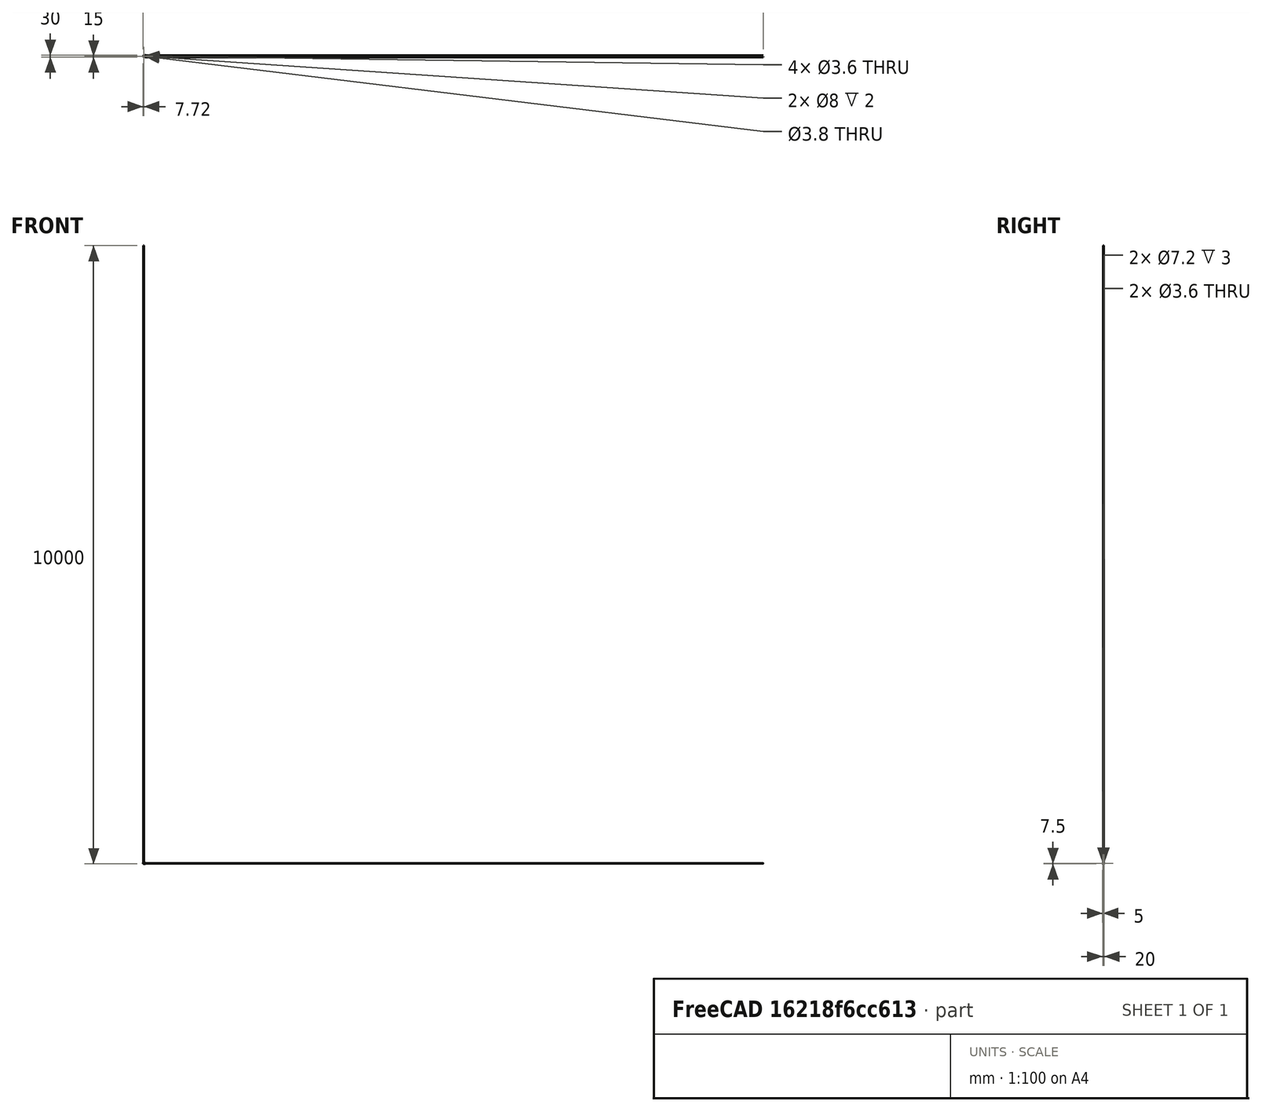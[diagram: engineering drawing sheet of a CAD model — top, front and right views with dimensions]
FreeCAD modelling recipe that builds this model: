
FCSTD DOCUMENT  (FreeCAD 0.15R4671 (Git))
Label: BedLevelingBracket
License: All rights reserved
LicenseURL: http://en.wikipedia.org/wiki/All_rights_reserved
objects: Sketcher::SketchObject×7, PartDesign::Pocket×5, Mesh::Feature×3, PartDesign::Fillet×3, PartDesign::Pad×2, Part::Feature×1
note: 25 computed .brp shape members not serialized (recipe doc carries the construction recipe); baked Part::Feature solids carry a one-line shape summary decoded from their .brp

FEATURE [Mesh::Feature] HexNutStyle1_M
  Placement = pos=(14.21,22,-108.55) rot=(0,0,1;0rad)
FEATURE [Part::Feature] Part__Feature  label="BedLevelingKnob"
  Placement = pos=(0,0,6) rot=(0,0,1;0rad)
  shape: bbox 15.67 x 15.67 x 5.638 mm, 113 faces (baked)
FEATURE [Mesh::Feature] SocketHeadCapScrew_M3x  label="SocketHeadCapScrew_M3x16"
  Placement = pos=(-8.5,22,-108) rot=(0,0,1;0rad)
FEATURE [Mesh::Feature] HexNutStyle1_M001
  Placement = pos=(14.21,22,-102.55) rot=(0,0,1;0rad)
FEATURE [Sketcher::SketchObject] Sketch
  sketch-geometry (4):
    g0: LineSegment StartX=-5 StartY=5 StartZ=0 EndX=21 EndY=5 EndZ=0
    g1: LineSegment StartX=21 StartY=5 StartZ=0 EndX=21 EndY=-5 EndZ=0
    g2: LineSegment StartX=21 StartY=-5 StartZ=0 EndX=-5 EndY=-5 EndZ=0
    g3: LineSegment StartX=-5 StartY=-5 StartZ=0 EndX=-5 EndY=5 EndZ=0
  constraints (8):
    c: Coincident(g0,g1)
    c: Coincident(g1,g2)
    c: Coincident(g2,g3)
    c: Coincident(g3,g0)
    c: Horizontal(g0)
    c: Horizontal(g2)
    c: Vertical(g1)
    c: Vertical(g3)
FEATURE [PartDesign::Pad] Pad
  Length = 15
  Length2 = 100
  Sketch = -> Sketch
  Type = 0
FEATURE [Sketcher::SketchObject] Sketch001
  Placement = pos=(0,-5,0) rot=(1,0,0;1.5708rad)
  Support = -> Pad [Face3]
  sketch-geometry (4):
    g0: LineSegment StartX=-9 StartY=11 StartZ=0 EndX=9 EndY=11 EndZ=0
    g1: LineSegment StartX=9 StartY=11 StartZ=0 EndX=9 EndY=4.5 EndZ=0
    g2: LineSegment StartX=9 StartY=4.5 StartZ=0 EndX=-9 EndY=4.5 EndZ=0
    g3: LineSegment StartX=-9 StartY=4.5 StartZ=0 EndX=-9 EndY=11 EndZ=0
  constraints (8):
    c: Coincident(g0,g1)
    c: Coincident(g1,g2)
    c: Coincident(g2,g3)
    c: Coincident(g3,g0)
    c: Horizontal(g0)
    c: Horizontal(g2)
    c: Vertical(g1)
    c: Vertical(g3)
FEATURE [PartDesign::Pocket] Pocket
  Length = 5
  Sketch = -> Sketch001
  Type = 1
FEATURE [PartDesign::Fillet] Fillet
  Base = -> Pocket [Edge24,Edge8,Edge4,Edge17]
  Radius = 4.99
FEATURE [Sketcher::SketchObject] Sketch002
  Placement = pos=(0,0,0) rot=(1,0,0;3.14159rad)
  Support = -> Fillet [Face2]
  sketch-geometry (1):
    g0: Circle CenterX=0 CenterY=0 CenterZ=0 NormalX=0 NormalY=0 NormalZ=1 Radius=1.8
  constraints (2):
    c: Coincident(g0,g-1)
    c: Radius(g0) = 1.8
FEATURE [PartDesign::Pocket] Pocket001
  Length = 5
  Sketch = -> Sketch002
  Type = 1
FEATURE [Sketcher::SketchObject] Sketch003
  Placement = pos=(0,0,15) rot=(0,0,1;0rad)
  Support = -> Pocket001 [Face6]
  sketch-geometry (1):
    g0: Circle CenterX=0 CenterY=0 CenterZ=0 NormalX=0 NormalY=0 NormalZ=1 Radius=4
  constraints (1):
    c: Coincident(g0,g-1)
FEATURE [PartDesign::Pocket] Pocket002
  Length = 2
  Sketch = -> Sketch003
  Type = 0
FEATURE [Sketcher::SketchObject] Sketch004
  Placement = pos=(21,0,0) rot=(0.57735,0.57735,0.57735;2.0944rad)
  Support = -> Pocket002 [Face4]
  sketch-geometry (4):
    g0: LineSegment StartX=-15 StartY=15 StartZ=0 EndX=15 EndY=15 EndZ=0
    g1: LineSegment StartX=15 StartY=15 StartZ=0 EndX=15 EndY=0 EndZ=0
    g2: LineSegment StartX=15 StartY=0 StartZ=0 EndX=-15 EndY=0 EndZ=0
    g3: LineSegment StartX=-15 StartY=0 StartZ=0 EndX=-15 EndY=15 EndZ=0
  constraints (11):
    c: Coincident(g0,g1)
    c: Coincident(g1,g2)
    c: Coincident(g2,g3)
    c: Coincident(g3,g0)
    c: Horizontal(g0)
    c: Horizontal(g2)
    c: Vertical(g1)
    c: Vertical(g3)
    c: PointOnObject(g1,g-1)
    c: DistanceX(g2,g1) = 30
    c: DistanceX(g-1,g2) = -15
FEATURE [PartDesign::Pad] Pad001
  Length = 7
  Length2 = 100
  Sketch = -> Sketch004
  Type = 0
FEATURE [Sketcher::SketchObject] Sketch005
  Placement = pos=(21,0,0) rot=(0.57735,-0.57735,-0.57735;2.0944rad)
  Support = -> Pad001 [Face17]
  sketch-geometry (2):
    g0: Circle CenterX=-10 CenterY=7.5 CenterZ=0 NormalX=0 NormalY=0 NormalZ=1 Radius=1.8
    g1: Circle CenterX=10 CenterY=7.5 CenterZ=0 NormalX=0 NormalY=0 NormalZ=1 Radius=1.8
  constraints (2):
    c: Radius(g1) = 1.8
    c: Equal(g1,g0)
FEATURE [PartDesign::Pocket] Pocket003
  Length = 5
  Sketch = -> Sketch005
  Type = 1
FEATURE [Sketcher::SketchObject] Sketch006
  Placement = pos=(21,0,0) rot=(0.57735,-0.57735,-0.57735;2.0944rad)
  Support = -> Pocket003 [Face13]
  sketch-geometry (2):
    g0: Circle CenterX=-10 CenterY=7.5 CenterZ=0 NormalX=0 NormalY=0 NormalZ=1 Radius=3.6
    g1: Circle CenterX=10 CenterY=7.5 CenterZ=0 NormalX=0 NormalY=0 NormalZ=1 Radius=3.6
  constraints (2):
    c: Radius(g1) = 3.6
    c: Equal(g1,g0)
FEATURE [PartDesign::Pocket] Pocket004
  Length = 3
  Sketch = -> Sketch006
  Type = 0
FEATURE [PartDesign::Fillet] Fillet001
  Base = -> Pocket004 [Edge10,Edge37,Edge12,Edge43]
  Radius = 4
FEATURE [PartDesign::Fillet] Fillet002  label="BedLevelingBracket"
  Base = -> Fillet001 [Edge13,Edge40]
  Radius = 1
